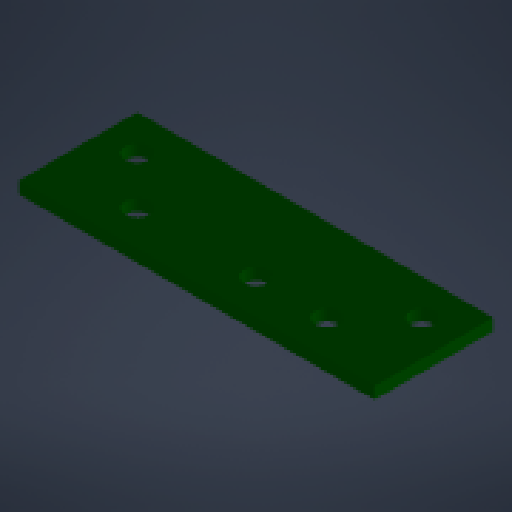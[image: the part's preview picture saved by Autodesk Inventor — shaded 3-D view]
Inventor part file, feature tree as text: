
AUTODESK INVENTOR PART (.ipt)
format: ipt  version: 2024 (Build 280153000, 153)  size: 134,656 bytes
history: native  units: mm
features: reference x10, other x6, extrude x1, sketch x1
ambient origin geometry x8: Origin, YZ Plane, XZ Plane, XY Plane, X Axis, Y Axis, Z Axis, Center Point
bodies: Body1 (feature_tree)
feature tree (18):
  other  "Твердое тело1"
  extrude  "Выдавливание1"  Depth=2.0mm TaperAngle=0.0deg
  sketch  "Эскиз1"
  reference  "Ссылка1"
  reference  "Ссылка2"
  reference  "Ссылка3"
  reference  "Ссылка4"
  reference  "Ссылка5"
  reference  "Ссылка6"
  reference  "Ссылка7"
  reference  "Ссылка8"
  reference  "Ссылка9"
  reference  "Ссылка10"
  parser-record x1  (decoder bookkeeping rows leaked as tree rows — omitted from the tree; the rows remain in map.json)
  other  "base_assembly.iam"
  other  "upper_plate:1"
  other  "square_box_side_section:1"
  other  "square_box_section:1"
note: 1 file-system path scrubbed to <path> (originals preserved in map.json)
